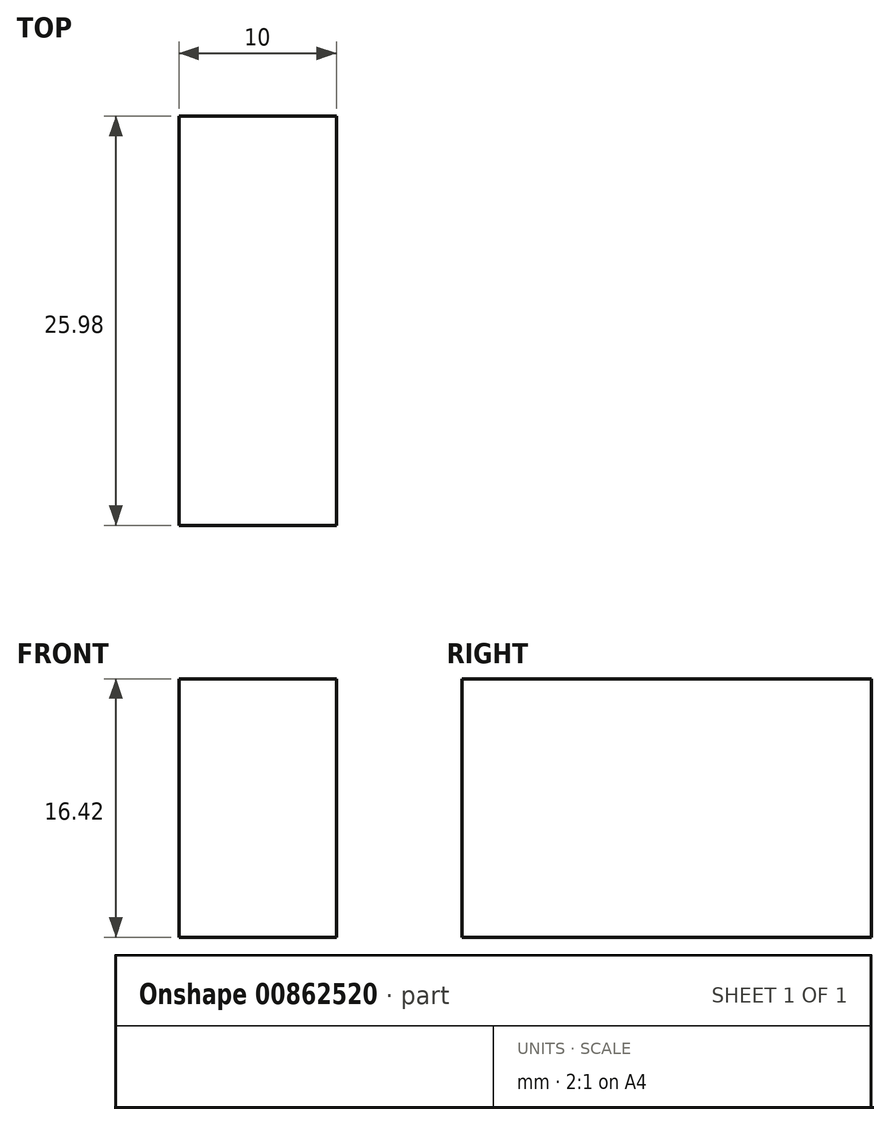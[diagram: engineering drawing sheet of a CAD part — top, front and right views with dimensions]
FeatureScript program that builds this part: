
annotation { "Feature Type Name" : "Feature", "Feature Type Description" : "" }
export const myFeature = defineFeature(function(context is Context, id is Id, definition is map)
    precondition{}
    {
        {
            var Q0;
            Q0=qCreatedBy(makeId("Right.planeOp"),FACE);
            var sketch = newSketch(context, id + "F0", { "sketchPlane" : qUnion([Q0])});
            skLineSegment(sketch, "E0.bottom", {"start": v(-59.1, 56.47) * mm, "end": v(-33.12, 56.47) * mm});
            skLineSegment(sketch, "E0.top", {"start": v(-59.1, 40.05) * mm, "end": v(-33.12, 40.05) * mm});
            skLineSegment(sketch, "E0.left", {"start": v(-59.1, 56.47) * mm, "end": v(-59.1, 40.05) * mm});
            skLineSegment(sketch, "E0.right", {"start": v(-33.12, 56.47) * mm, "end": v(-33.12, 40.05) * mm});
            skSolve(sketch);
        }
        {
            var Q0;
            Q0 = qSketchRegion(id + "F0", true);
            extrude(context, id + "F1", {"entities" : qUnion([Q0]), "depth" : 10 * mm, "offsetDistance" : 25.4 * mm});
        }
    });
